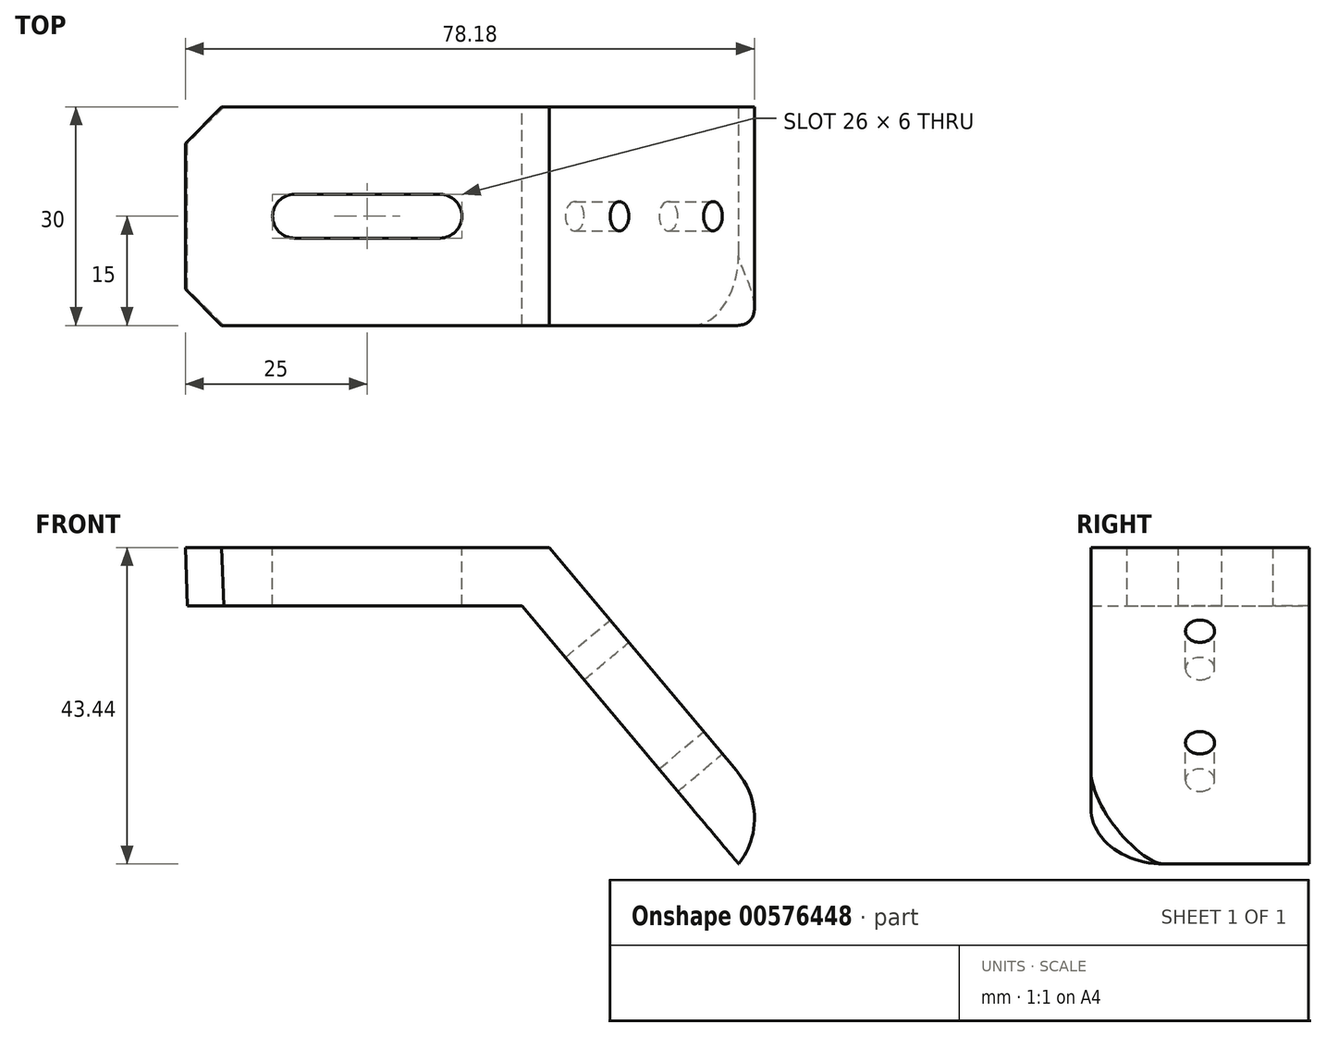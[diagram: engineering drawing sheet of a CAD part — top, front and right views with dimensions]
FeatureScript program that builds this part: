
annotation { "Feature Type Name" : "Feature", "Feature Type Description" : "" }
export const myFeature = defineFeature(function(context is Context, id is Id, definition is map)
    precondition{}
    {
        {
            var Q0;
            Q0=qCreatedBy(makeId("Front.planeOp"),FACE);
            var sketch = newSketch(context, id + "F0", { "sketchPlane" : qUnion([Q0])});
            skLineSegment(sketch, "E0", {"start": v(0, 0) * mm, "end": v(46, 0) * mm});
            skLineSegment(sketch, "E1", {"start": v(46, 0) * mm, "end": v(75.74, -35.44) * mm});
            skLineSegment(sketch, "E2.0", {"start": v(49.73, 8) * mm, "end": v(81.87, -30.3) * mm});
            skLineSegment(sketch, "E2.1", {"start": v(-0.27, 8) * mm, "end": v(49.73, 8) * mm});
            skLineSegment(sketch, "E3", {"start": v(-0.27, 8) * mm, "end": v(0, 0) * mm});
            skLineSegment(sketch, "E4", {"start": v(81.87, -30.3) * mm, "end": v(75.74, -35.44) * mm});
            skSolve(sketch);
        }
        {
            var Q0;
            Q0 = qSketchRegion(id + "F0", true);
            extrude(context, id + "F1", {"entities" : qUnion([Q0]), "endBound" : BoundingType.SYMMETRIC, "depth" : 30 * mm, "offsetDistance" : 25 * mm});
        }
        {
            var Q0;
            Q0=makeQuery(id+"F1.opExtrude","SWEPT_FACE",FACE,{"disambiguationData":[OSD([sQuery(id+"F0.wireOp",EDGE,"E2.1")])]});
            var sketch = newSketch(context, id + "F2", { "sketchPlane" : qUnion([Q0])});
            skLineSegment(sketch, "E5", {"start": v(14.73, 0) * mm, "end": v(34.73, 0) * mm});
            skArc(sketch, "E6.0.startCap", {"start": v(14.73, -3) * mm, "mid": v(11.73, 0) * mm, "end": v(14.73, 3) * mm});
            skArc(sketch, "E6.0.endCap", {"start": v(34.73, 3) * mm, "mid": v(37.73, 0) * mm, "end": v(34.73, -3) * mm});
            skLineSegment(sketch, "E6.0.left", {"start": v(14.73, 3) * mm, "end": v(34.73, 3) * mm});
            skLineSegment(sketch, "E6.0.right", {"start": v(14.73, -3) * mm, "end": v(34.73, -3) * mm});
            skSolve(sketch);
        }
        {
            var Q0;
            Q0 = qSketchRegion(id + "F2", true);
            extrude(context, id + "F3", {"entities" : qUnion([Q0]), "operationType" : NewBodyOperationType.REMOVE, "endBound" : BoundingType.THROUGH_ALL, "oppositeDirection" : true, "depth" : 25 * mm, "offsetDistance" : 25 * mm});
        }
        {
            var Q0;
            Q0=makeQuery(id+"F1.opExtrude","SWEPT_FACE",FACE,{"disambiguationData":[OSD([sQuery(id+"F0.wireOp",EDGE,"E2.0")])]});
            var sketch = newSketch(context, id + "F4", { "sketchPlane" : qUnion([Q0])});
            skPoint(sketch, "E7", {"position": v(0, -40.84) * mm});
            skPoint(sketch, "E8", {"position": v(0, -60.84) * mm});
            skSolve(sketch);
        }
        {
            var Q0;
            Q0=sQuery(id+"F4.wireOp",VERTEX,"E7");
            var Q1;
            Q1=sQuery(id+"F4.wireOp",VERTEX,"E8");
            var Q2;
            Q2=makeQuery(id+"F1.opExtrude","SWEPT_BODY",BODY,{"disambiguationData":[OSD([sQuery(id+"F0.wireOp",EDGE,"E0"),sQuery(id+"F0.wireOp",EDGE,"E1"),sQuery(id+"F0.wireOp",EDGE,"E2.0"),sQuery(id+"F0.wireOp",EDGE,"E2.1"),sQuery(id+"F0.wireOp",EDGE,"E3"),sQuery(id+"F0.wireOp",EDGE,"E4")])]});
            hole(context, id + "F5", {"style" : HoleStyle.SIMPLE, "endStyle" : HoleEndStyle.THROUGH, "holeDiameter" : 4 * mm, "isTappedThrough" : true, "tappedDepth" : 12 * mm, "tapClearance" : 3, "locations" : qUnion([Q0, Q1]), "scope" : qUnion([Q2])});
        }
        {
            var Q0;
            Q0=makeQuery(id+"F1.opExtrude","SWEPT_EDGE",EDGE,{"disambiguationData":[OSD([sQuery(id+"F0.wireOp",EDGE,"E2.0"),sQuery(id+"F0.wireOp",EDGE,"E4")])]});
            var Q1;
            Q1=makeQuery(id+"F1.opExtrude","CAP_EDGE",EDGE,{"disambiguationData":[OSD([sQuery(id+"F0.wireOp",EDGE,"E4")])],"isStart":false});
            fillet(context, id + "F6", {"entities" : qUnion([Q0, Q1]), "radius" : 10 * mm, "tangentPropagation" : true, "allowEdgeOverflow" : false});
        }
        {
            var Q0;
            Q0=makeQuery(id+"F1.opExtrude","CAP_EDGE",EDGE,{"disambiguationData":[OSD([sQuery(id+"F0.wireOp",EDGE,"E3")])],"isStart":false});
            var Q1;
            Q1=makeQuery(id+"F1.opExtrude","CAP_EDGE",EDGE,{"disambiguationData":[OSD([sQuery(id+"F0.wireOp",EDGE,"E3")])],"isStart":true});
            chamfer(context, id + "F7", {"entities" : qUnion([Q0, Q1]), "width" : 5 * mm, "tangentPropagation" : true});
        }
    });
